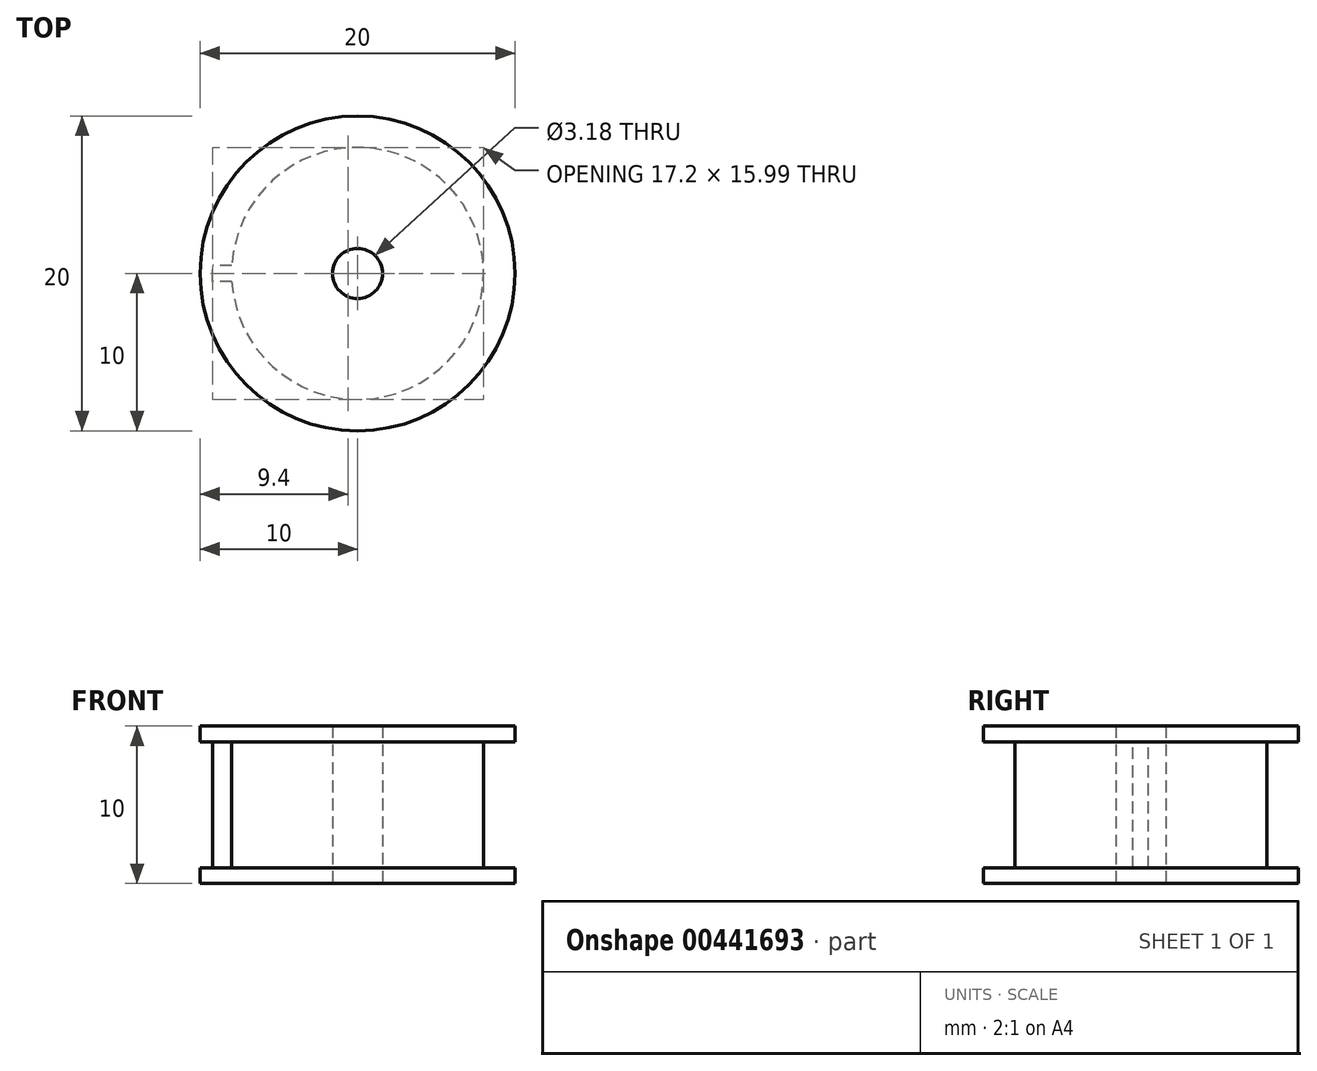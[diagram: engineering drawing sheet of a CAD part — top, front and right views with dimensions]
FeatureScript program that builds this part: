
annotation { "Feature Type Name" : "Feature", "Feature Type Description" : "" }
export const myFeature = defineFeature(function(context is Context, id is Id, definition is map)
    precondition{}
    {
        {
            var Q0;
            Q0=qCreatedBy(makeId("Top.planeOp"),FACE);
            var sketch = newSketch(context, id + "F0", { "sketchPlane" : qUnion([Q0])});
            skCircle(sketch, "E0", {"center": v(0, 0) * mm, "radius": 1.6 * mm});
            skCircle(sketch, "E1", {"center": v(0, 0) * mm, "radius": 10 * mm});
            skLineSegment(sketch, "E2", {"start": v(0, 20.95) * mm, "end": v(0, -16.63) * mm, "construction": true});
            skLineSegment(sketch, "E3", {"start": v(-2, 9.8) * mm, "end": v(-1, 12) * mm});
            skLineSegment(sketch, "E4", {"start": v(-1, 12) * mm, "end": v(1, 12) * mm});
            skLineSegment(sketch, "E5", {"start": v(1, 12) * mm, "end": v(2, 9.8) * mm});
            skArc(sketch, "E6", {"start": v(2, 9.8) * mm, "mid": v(0, 10) * mm, "end": v(-2, 9.8) * mm});
            skSolve(sketch);
        }
        {
            var Q0;
            Q0=makeQuery(id+"F0.imprint","IMPRINT",FACE,{"disambiguationData":[TD([[makeQuery(id+"F0.imprint","IMPRINT",EDGE,{"derivedFrom":sQuery(id+"F0.wireOp",EDGE,"E0")}),-1.0]])]});
            extrude(context, id + "F1", {"entities" : qUnion([Q0]), "endBound" : BoundingType.SYMMETRIC, "depth" : 10 * mm});
        }
        {
            var Q0;
            Q0=qCreatedBy(makeId("Front.planeOp"),FACE);
            var sketch = newSketch(context, id + "F2", { "sketchPlane" : qUnion([Q0])});
            skLineSegment(sketch, "E7", {"start": v(-10, 5) * mm, "end": v(-10, 4) * mm});
            skLineSegment(sketch, "E8", {"start": v(-10, 4) * mm, "end": v(-8, 4) * mm});
            skLineSegment(sketch, "E9", {"start": v(-8, 4) * mm, "end": v(-8, -4) * mm});
            skLineSegment(sketch, "E10", {"start": v(-8, -4) * mm, "end": v(-10, -4) * mm});
            skLineSegment(sketch, "E11", {"start": v(-10, -4) * mm, "end": v(-10, -5) * mm});
            skLineSegment(sketch, "E12", {"start": v(-19.06, 0) * mm, "end": v(0.57, 0) * mm, "construction": true});
            skLineSegment(sketch, "E13", {"start": v(-10, 6.07) * mm, "end": v(-10, -6.77) * mm, "construction": true});
            skLineSegment(sketch, "E14", {"start": v(0, 6.53) * mm, "end": v(0, -7.99) * mm, "construction": true});
            skLineSegment(sketch, "E15", {"start": v(-10, 4) * mm, "end": v(-10, -4) * mm});
            skSolve(sketch);
        }
        {
            var Q0;
            Q0 = qSketchRegion(id + "F2", true);
            var Q1;
            Q1=makeQuery(id+"F1.opExtrude","CAP_EDGE",EDGE,{"disambiguationData":[OSD([sQuery(id+"F0.wireOp",EDGE,"E1")])],"isStart":true});
            sweep(context, id + "F3", {"operationType" : NewBodyOperationType.REMOVE, "profiles" : qUnion([Q0]), "path" : qUnion([Q1])});
        }
        {
            var Q0;
            Q0=qCreatedBy(makeId("Front.planeOp"),FACE);
            var sketch = newSketch(context, id + "F4", { "sketchPlane" : qUnion([Q0])});
            skLineSegment(sketch, "E16", {"start": v(-9.2, 4) * mm, "end": v(-9.2, -4) * mm});
            skLineSegment(sketch, "E17", {"start": v(-9.2, -4) * mm, "end": v(-5.86, -4) * mm});
            skLineSegment(sketch, "E18", {"start": v(-5.86, -4) * mm, "end": v(-5.86, 4) * mm});
            skLineSegment(sketch, "E19", {"start": v(-5.86, 4) * mm, "end": v(-9.2, 4) * mm});
            skLineSegment(sketch, "E20", {"start": v(-15.16, 0) * mm, "end": v(12.88, 0) * mm, "construction": true});
            skLineSegment(sketch, "E21", {"start": v(-8, 4) * mm, "end": v(-8, -4) * mm});
            skSolve(sketch);
        }
        {
            var Q0;
            Q0 = qSketchRegion(id + "F4", true);
            extrude(context, id + "F5", {"entities" : qUnion([Q0]), "operationType" : NewBodyOperationType.ADD, "endBound" : BoundingType.SYMMETRIC, "depth" : 1 * mm, "offsetDistance" : 25 * mm});
        }
    });
